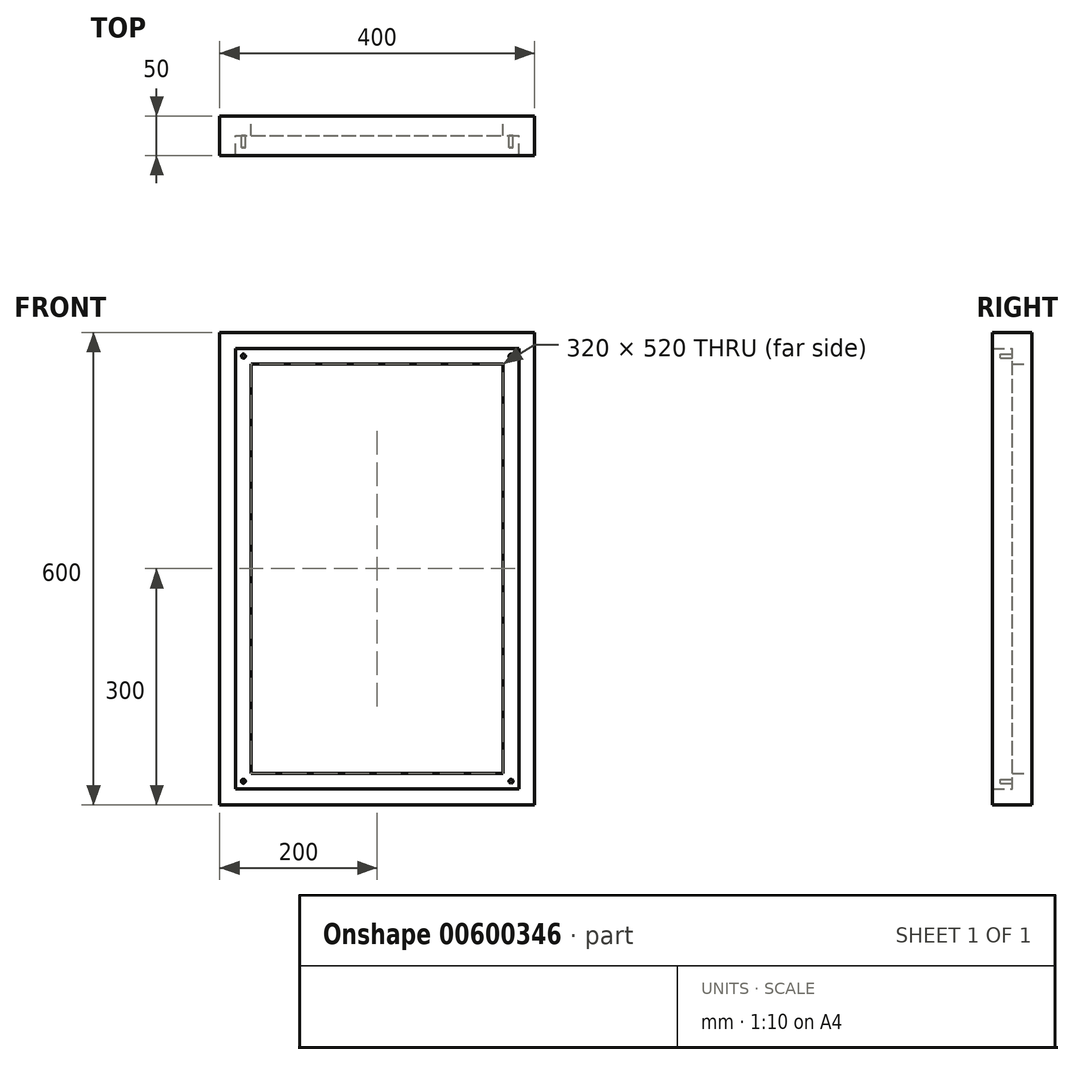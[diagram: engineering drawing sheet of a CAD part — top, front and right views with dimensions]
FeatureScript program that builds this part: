
annotation { "Feature Type Name" : "Feature", "Feature Type Description" : "" }
export const myFeature = defineFeature(function(context is Context, id is Id, definition is map)
    precondition{}
    {
        {
            var Q0;
            Q0=qCreatedBy(makeId("Front.planeOp"),FACE);
            var sketch = newSketch(context, id + "F0", { "sketchPlane" : qUnion([Q0])});
            skLineSegment(sketch, "E0.bottom", {"start": v(0, 0) * mm, "end": v(400, 0) * mm});
            skLineSegment(sketch, "E0.top", {"start": v(0, 600) * mm, "end": v(400, 600) * mm});
            skLineSegment(sketch, "E0.left", {"start": v(0, 0) * mm, "end": v(0, 600) * mm});
            skLineSegment(sketch, "E0.right", {"start": v(400, 0) * mm, "end": v(400, 600) * mm});
            skLineSegment(sketch, "E1.0", {"start": v(0, 580) * mm, "end": v(400, 580) * mm});
            skLineSegment(sketch, "E2.0", {"start": v(20, 0) * mm, "end": v(20, 600) * mm});
            skLineSegment(sketch, "E3.0", {"start": v(380, 0) * mm, "end": v(380, 600) * mm});
            skLineSegment(sketch, "E4.0", {"start": v(0, 560) * mm, "end": v(400, 560) * mm});
            skLineSegment(sketch, "E5.0", {"start": v(360, 0) * mm, "end": v(360, 600) * mm});
            skLineSegment(sketch, "E6.0", {"start": v(40, 0) * mm, "end": v(40, 600) * mm});
            skLineSegment(sketch, "E7.0", {"start": v(0, 20) * mm, "end": v(400, 20) * mm});
            skLineSegment(sketch, "E8.0", {"start": v(0, 40) * mm, "end": v(400, 40) * mm});
            skCircle(sketch, "E9.MirrorC", {"center": v(370, 570) * mm, "radius": 2.5 * mm});
            skPoint(sketch, "E10", {"position": v(20, 580) * mm});
            skPoint(sketch, "E11", {"position": v(40, 580) * mm});
            skPoint(sketch, "E12", {"position": v(40, 560) * mm});
            skPoint(sketch, "E13", {"position": v(20, 560) * mm});
            skCircle(sketch, "E14", {"center": v(30, 570) * mm, "radius": 2.5 * mm});
            skPoint(sketch, "E15", {"position": v(20, 40) * mm});
            skPoint(sketch, "E16", {"position": v(40, 40) * mm});
            skPoint(sketch, "E17", {"position": v(40, 20) * mm});
            skPoint(sketch, "E18", {"position": v(20, 20) * mm});
            skCircle(sketch, "E19", {"center": v(30, 30) * mm, "radius": 2.5 * mm});
            skPoint(sketch, "E20", {"position": v(360, 40) * mm});
            skPoint(sketch, "E21", {"position": v(380, 40) * mm});
            skPoint(sketch, "E22", {"position": v(380, 20) * mm});
            skPoint(sketch, "E23", {"position": v(360, 20) * mm});
            skCircle(sketch, "E24", {"center": v(370, 30) * mm, "radius": 2.5 * mm});
            skSolve(sketch);
        }
        {
            var Q0;
            {var subQ0=sQuery(id+"F0.wireOp",EDGE,"E0.right");var subQ1=sQuery(id+"F0.wireOp",EDGE,"E0.bottom");var subQ2=makeQuery(id+"F0.imprint","INTERSECT",VERTEX,{"derivedFrom":[subQ1,subQ0]});Q0=makeQuery(id+"F0.imprint","IMPRINT",FACE,{"disambiguationData":[TD([[makeQuery(id+"F0.imprint","IMPRINT",EDGE,{"disambiguationData":[TD([[subQ2,1.0]])],"derivedFrom":subQ1}),1.0]])]});}
            var Q1;
            {var subQ0=sQuery(id+"F0.wireOp",EDGE,"E3.0");var subQ1=sQuery(id+"F0.wireOp",EDGE,"E0.bottom");var subQ2=makeQuery(id+"F0.imprint","INTERSECT",VERTEX,{"derivedFrom":[subQ1,subQ0]});Q1=makeQuery(id+"F0.imprint","IMPRINT",FACE,{"disambiguationData":[TD([[makeQuery(id+"F0.imprint","IMPRINT",EDGE,{"disambiguationData":[TD([[subQ2,1.0]])],"derivedFrom":subQ1}),1.0]])]});}
            var Q2;
            {var subQ0=sQuery(id+"F0.wireOp",EDGE,"E5.0");var subQ1=sQuery(id+"F0.wireOp",EDGE,"E0.bottom");var subQ2=makeQuery(id+"F0.imprint","INTERSECT",VERTEX,{"derivedFrom":[subQ1,subQ0]});Q2=makeQuery(id+"F0.imprint","IMPRINT",FACE,{"disambiguationData":[TD([[makeQuery(id+"F0.imprint","IMPRINT",EDGE,{"disambiguationData":[TD([[subQ2,1.0]])],"derivedFrom":subQ1}),1.0]])]});}
            var Q3;
            {var subQ0=sQuery(id+"F0.wireOp",EDGE,"E4.0");var subQ1=sQuery(id+"F0.wireOp",EDGE,"E0.right");var subQ2=makeQuery(id+"F0.imprint","INTERSECT",VERTEX,{"derivedFrom":[subQ1,subQ0]});Q3=makeQuery(id+"F0.imprint","IMPRINT",FACE,{"disambiguationData":[TD([[makeQuery(id+"F0.imprint","IMPRINT",EDGE,{"disambiguationData":[TD([[subQ2,1.0]])],"derivedFrom":subQ1}),1.0]])]});}
            var Q4;
            {var subQ0=sQuery(id+"F0.wireOp",EDGE,"E7.0");var subQ1=sQuery(id+"F0.wireOp",EDGE,"E0.right");var subQ2=makeQuery(id+"F0.imprint","INTERSECT",VERTEX,{"derivedFrom":[subQ1,subQ0]});Q4=makeQuery(id+"F0.imprint","IMPRINT",FACE,{"disambiguationData":[TD([[makeQuery(id+"F0.imprint","IMPRINT",EDGE,{"disambiguationData":[TD([[subQ2,-1.0]])],"derivedFrom":subQ1}),1.0]])]});}
            var Q5;
            {var subQ0=sQuery(id+"F0.wireOp",EDGE,"E2.0");var subQ1=sQuery(id+"F0.wireOp",EDGE,"E0.bottom");var subQ2=makeQuery(id+"F0.imprint","INTERSECT",VERTEX,{"derivedFrom":[subQ1,subQ0]});Q5=makeQuery(id+"F0.imprint","IMPRINT",FACE,{"disambiguationData":[TD([[makeQuery(id+"F0.imprint","IMPRINT",EDGE,{"disambiguationData":[TD([[subQ2,-1.0]])],"derivedFrom":subQ1}),1.0]])]});}
            var Q6;
            {var subQ0=sQuery(id+"F0.wireOp",EDGE,"E0.left");var subQ1=sQuery(id+"F0.wireOp",EDGE,"E0.bottom");var subQ2=makeQuery(id+"F0.imprint","INTERSECT",VERTEX,{"derivedFrom":[subQ1,subQ0]});Q6=makeQuery(id+"F0.imprint","IMPRINT",FACE,{"disambiguationData":[TD([[makeQuery(id+"F0.imprint","IMPRINT",EDGE,{"disambiguationData":[TD([[subQ2,-1.0]])],"derivedFrom":subQ1}),1.0]])]});}
            var Q7;
            {var subQ0=sQuery(id+"F0.wireOp",EDGE,"E7.0");var subQ1=sQuery(id+"F0.wireOp",EDGE,"E0.left");var subQ2=makeQuery(id+"F0.imprint","INTERSECT",VERTEX,{"derivedFrom":[subQ1,subQ0]});Q7=makeQuery(id+"F0.imprint","IMPRINT",FACE,{"disambiguationData":[TD([[makeQuery(id+"F0.imprint","IMPRINT",EDGE,{"disambiguationData":[TD([[subQ2,-1.0]])],"derivedFrom":subQ1}),-1.0]])]});}
            var Q8;
            {var subQ0=sQuery(id+"F0.wireOp",EDGE,"E4.0");var subQ1=sQuery(id+"F0.wireOp",EDGE,"E0.left");var subQ2=makeQuery(id+"F0.imprint","INTERSECT",VERTEX,{"derivedFrom":[subQ1,subQ0]});Q8=makeQuery(id+"F0.imprint","IMPRINT",FACE,{"disambiguationData":[TD([[makeQuery(id+"F0.imprint","IMPRINT",EDGE,{"disambiguationData":[TD([[subQ2,1.0]])],"derivedFrom":subQ1}),-1.0]])]});}
            var Q9;
            {var subQ0=sQuery(id+"F0.wireOp",EDGE,"E1.0");var subQ1=sQuery(id+"F0.wireOp",EDGE,"E0.right");var subQ2=makeQuery(id+"F0.imprint","INTERSECT",VERTEX,{"derivedFrom":[subQ1,subQ0]});Q9=makeQuery(id+"F0.imprint","IMPRINT",FACE,{"disambiguationData":[TD([[makeQuery(id+"F0.imprint","IMPRINT",EDGE,{"disambiguationData":[TD([[subQ2,1.0]])],"derivedFrom":subQ1}),1.0]])]});}
            var Q10;
            {var subQ0=sQuery(id+"F0.wireOp",EDGE,"E0.right");var subQ1=sQuery(id+"F0.wireOp",EDGE,"E0.top");var subQ2=makeQuery(id+"F0.imprint","INTERSECT",VERTEX,{"derivedFrom":[subQ1,subQ0]});Q10=makeQuery(id+"F0.imprint","IMPRINT",FACE,{"disambiguationData":[TD([[makeQuery(id+"F0.imprint","IMPRINT",EDGE,{"disambiguationData":[TD([[subQ2,1.0]])],"derivedFrom":subQ1}),-1.0]])]});}
            var Q11;
            {var subQ0=sQuery(id+"F0.wireOp",EDGE,"E3.0");var subQ1=sQuery(id+"F0.wireOp",EDGE,"E0.top");var subQ2=makeQuery(id+"F0.imprint","INTERSECT",VERTEX,{"derivedFrom":[subQ1,subQ0]});Q11=makeQuery(id+"F0.imprint","IMPRINT",FACE,{"disambiguationData":[TD([[makeQuery(id+"F0.imprint","IMPRINT",EDGE,{"disambiguationData":[TD([[subQ2,1.0]])],"derivedFrom":subQ1}),-1.0]])]});}
            var Q12;
            {var subQ0=sQuery(id+"F0.wireOp",EDGE,"E5.0");var subQ1=sQuery(id+"F0.wireOp",EDGE,"E0.top");var subQ2=makeQuery(id+"F0.imprint","INTERSECT",VERTEX,{"derivedFrom":[subQ1,subQ0]});Q12=makeQuery(id+"F0.imprint","IMPRINT",FACE,{"disambiguationData":[TD([[makeQuery(id+"F0.imprint","IMPRINT",EDGE,{"disambiguationData":[TD([[subQ2,1.0]])],"derivedFrom":subQ1}),-1.0]])]});}
            var Q13;
            {var subQ0=sQuery(id+"F0.wireOp",EDGE,"E2.0");var subQ1=sQuery(id+"F0.wireOp",EDGE,"E0.top");var subQ2=makeQuery(id+"F0.imprint","INTERSECT",VERTEX,{"derivedFrom":[subQ1,subQ0]});Q13=makeQuery(id+"F0.imprint","IMPRINT",FACE,{"disambiguationData":[TD([[makeQuery(id+"F0.imprint","IMPRINT",EDGE,{"disambiguationData":[TD([[subQ2,-1.0]])],"derivedFrom":subQ1}),-1.0]])]});}
            var Q14;
            {var subQ0=sQuery(id+"F0.wireOp",EDGE,"E0.left");var subQ1=sQuery(id+"F0.wireOp",EDGE,"E0.top");var subQ2=makeQuery(id+"F0.imprint","INTERSECT",VERTEX,{"derivedFrom":[subQ1,subQ0]});Q14=makeQuery(id+"F0.imprint","IMPRINT",FACE,{"disambiguationData":[TD([[makeQuery(id+"F0.imprint","IMPRINT",EDGE,{"disambiguationData":[TD([[subQ2,-1.0]])],"derivedFrom":subQ1}),-1.0]])]});}
            var Q15;
            {var subQ0=sQuery(id+"F0.wireOp",EDGE,"E1.0");var subQ1=sQuery(id+"F0.wireOp",EDGE,"E0.left");var subQ2=makeQuery(id+"F0.imprint","INTERSECT",VERTEX,{"derivedFrom":[subQ1,subQ0]});Q15=makeQuery(id+"F0.imprint","IMPRINT",FACE,{"disambiguationData":[TD([[makeQuery(id+"F0.imprint","IMPRINT",EDGE,{"disambiguationData":[TD([[subQ2,1.0]])],"derivedFrom":subQ1}),-1.0]])]});}
            extrude(context, id + "F1", {"entities" : qUnion([Q0, Q1, Q2, Q3, Q4, Q5, Q6, Q7, Q8, Q9, Q10, Q11, Q12, Q13, Q14, Q15]), "depth" : 50 * mm, "offsetDistance" : 25 * mm});
        }
        {
            var Q0;
            Q0=makeQuery(id+"F0.imprint","IMPRINT",FACE,{"disambiguationData":[TD([[makeQuery(id+"F0.imprint","IMPRINT",EDGE,{"derivedFrom":sQuery(id+"F0.wireOp",EDGE,"E9.MirrorC")}),-1.0]])]});
            var Q1;
            {var subQ0=sQuery(id+"F0.wireOp",EDGE,"E6.0");var subQ1=sQuery(id+"F0.wireOp",EDGE,"E1.0");var subQ2=makeQuery(id+"F0.imprint","INTERSECT",VERTEX,{"derivedFrom":[subQ1,subQ0]});Q1=makeQuery(id+"F0.imprint","IMPRINT",FACE,{"disambiguationData":[TD([[makeQuery(id+"F0.imprint","IMPRINT",EDGE,{"disambiguationData":[TD([[subQ2,-1.0]])],"derivedFrom":subQ1}),-1.0]])]});}
            var Q2;
            {var subQ0=sQuery(id+"F0.wireOp",EDGE,"E8.0");var subQ1=sQuery(id+"F0.wireOp",EDGE,"E3.0");var subQ2=makeQuery(id+"F0.imprint","INTERSECT",VERTEX,{"derivedFrom":[subQ1,subQ0]});Q2=makeQuery(id+"F0.imprint","IMPRINT",FACE,{"disambiguationData":[TD([[makeQuery(id+"F0.imprint","IMPRINT",EDGE,{"disambiguationData":[TD([[subQ2,-1.0]])],"derivedFrom":subQ1}),1.0]])]});}
            var Q3;
            Q3=makeQuery(id+"F0.imprint","IMPRINT",FACE,{"disambiguationData":[TD([[makeQuery(id+"F0.imprint","IMPRINT",EDGE,{"derivedFrom":sQuery(id+"F0.wireOp",EDGE,"E14")}),-1.0]])]});
            var Q4;
            {var subQ0=sQuery(id+"F0.wireOp",EDGE,"E8.0");var subQ1=sQuery(id+"F0.wireOp",EDGE,"E2.0");var subQ2=makeQuery(id+"F0.imprint","INTERSECT",VERTEX,{"derivedFrom":[subQ1,subQ0]});Q4=makeQuery(id+"F0.imprint","IMPRINT",FACE,{"disambiguationData":[TD([[makeQuery(id+"F0.imprint","IMPRINT",EDGE,{"disambiguationData":[TD([[subQ2,-1.0]])],"derivedFrom":subQ1}),-1.0]])]});}
            var Q5;
            Q5=makeQuery(id+"F0.imprint","IMPRINT",FACE,{"disambiguationData":[TD([[makeQuery(id+"F0.imprint","IMPRINT",EDGE,{"derivedFrom":sQuery(id+"F0.wireOp",EDGE,"E19")}),-1.0]])]});
            var Q6;
            {var subQ0=sQuery(id+"F0.wireOp",EDGE,"E7.0");var subQ1=sQuery(id+"F0.wireOp",EDGE,"E5.0");var subQ2=makeQuery(id+"F0.imprint","INTERSECT",VERTEX,{"derivedFrom":[subQ1,subQ0]});Q6=makeQuery(id+"F0.imprint","IMPRINT",FACE,{"disambiguationData":[TD([[makeQuery(id+"F0.imprint","IMPRINT",EDGE,{"disambiguationData":[TD([[subQ2,-1.0]])],"derivedFrom":subQ1}),1.0]])]});}
            var Q7;
            Q7=makeQuery(id+"F0.imprint","IMPRINT",FACE,{"disambiguationData":[TD([[makeQuery(id+"F0.imprint","IMPRINT",EDGE,{"derivedFrom":sQuery(id+"F0.wireOp",EDGE,"E24")}),-1.0]])]});
            extrude(context, id + "F2", {"entities" : qUnion([Q0, Q1, Q2, Q3, Q4, Q5, Q6, Q7]), "operationType" : NewBodyOperationType.ADD, "depth" : 25 * mm, "offsetDistance" : 25 * mm});
        }
        {
            var Q0;
            Q0=makeQuery(id+"F0.imprint","IMPRINT",FACE,{"disambiguationData":[TD([[makeQuery(id+"F0.imprint","IMPRINT",EDGE,{"derivedFrom":sQuery(id+"F0.wireOp",EDGE,"E24")}),1.0]])]});
            var Q1;
            Q1=makeQuery(id+"F0.imprint","IMPRINT",FACE,{"disambiguationData":[TD([[makeQuery(id+"F0.imprint","IMPRINT",EDGE,{"derivedFrom":sQuery(id+"F0.wireOp",EDGE,"E19")}),1.0]])]});
            var Q2;
            Q2=makeQuery(id+"F0.imprint","IMPRINT",FACE,{"disambiguationData":[TD([[makeQuery(id+"F0.imprint","IMPRINT",EDGE,{"derivedFrom":sQuery(id+"F0.wireOp",EDGE,"E14")}),1.0]])]});
            var Q3;
            Q3=makeQuery(id+"F0.imprint","IMPRINT",FACE,{"disambiguationData":[TD([[makeQuery(id+"F0.imprint","IMPRINT",EDGE,{"derivedFrom":sQuery(id+"F0.wireOp",EDGE,"E9.MirrorC")}),1.0]])]});
            extrude(context, id + "F3", {"entities" : qUnion([Q0, Q1, Q2, Q3]), "operationType" : NewBodyOperationType.ADD, "depth" : 40 * mm, "offsetDistance" : 25 * mm});
        }
    });
